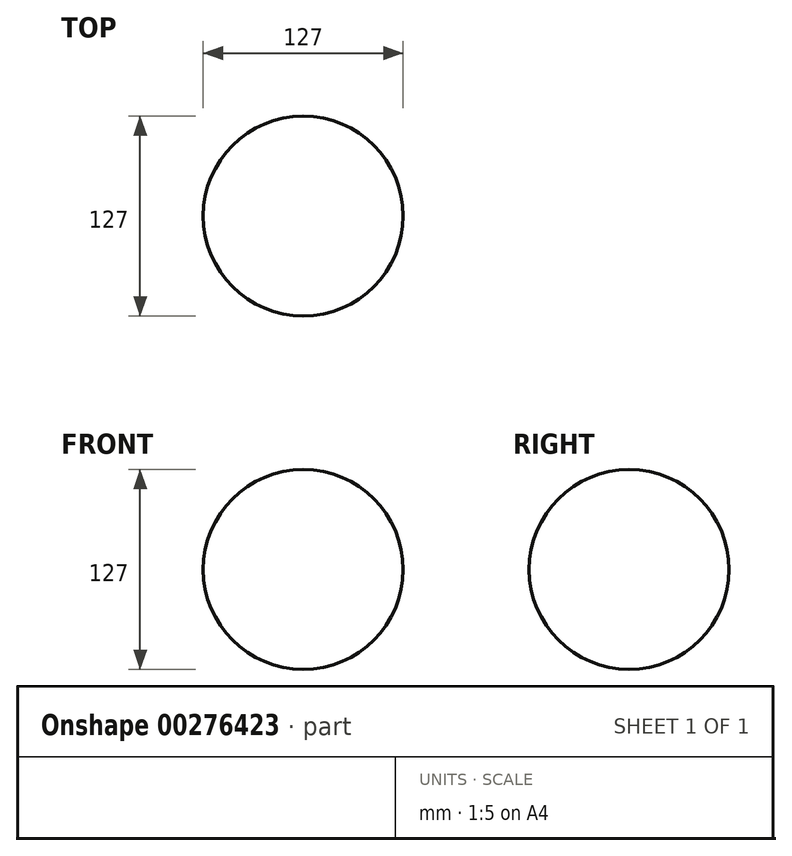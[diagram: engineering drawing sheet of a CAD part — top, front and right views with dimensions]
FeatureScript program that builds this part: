
annotation { "Feature Type Name" : "Feature", "Feature Type Description" : "" }
export const myFeature = defineFeature(function(context is Context, id is Id, definition is map)
    precondition{}
    {
        {
            var Q0;
            Q0=qCreatedBy(makeId("Top.planeOp"),FACE);
            var sketch = newSketch(context, id + "F0", { "sketchPlane" : qUnion([Q0])});
            skArc(sketch, "E0", {"start": v(0, -63.5) * mm, "mid": v(63.5, 0) * mm, "end": v(0, 63.5) * mm});
            skLineSegment(sketch, "E1", {"start": v(0, 71.88) * mm, "end": v(0, -68.92) * mm});
            skSolve(sketch);
        }
        {
            var Q0;
            Q0=sQuery(id+"F0.wireOp",EDGE,"E0");
            var Q1;
            Q1=sQuery(id+"F0.wireOp",EDGE,"E1");
            revolve(context, id + "F1", {"bodyType" : ToolBodyType.SURFACE, "surfaceEntities" : qUnion([Q0]), "axis" : qUnion([Q1]), "revolveType" : RevolveType.FULL});
        }
    });
